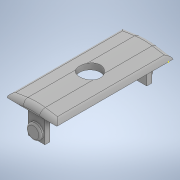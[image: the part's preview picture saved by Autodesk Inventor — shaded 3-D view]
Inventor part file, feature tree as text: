
AUTODESK INVENTOR PART (.ipt)
format: ipt  version: 2022 (Build 260153000, 153)  size: 212,480 bytes
history: native  units: mm
features: sketch x6, extrude x5, fillet x3, chamfer x2, mirror x1
ambient origin geometry x8: Origin, YZ Plane, XZ Plane, XY Plane, X Axis, Y Axis, Z Axis, Center Point
bodies: Solid1 (feature_tree)
feature tree (17):
  extrude  "Extrusion1"  Depth=70.0mm
  chamfer  "Chamfer1"  Distance=4.0mm
  chamfer  "Chamfer2"  Distance=2.0mm Angle=45.0deg
  fillet  "Fillet1"  Radius=35.0mm
  fillet  "Fillet2"  Radius=3.0mm
  extrude  "Extrusion2"  Depth=6.2mm
  extrude  "Extrusion3"  Depth=1.0mm
  extrude  "Extrusion4"  Depth=3.0mm
  fillet  "Fillet3"  Radius=10.0mm
  extrude  "Extrusion5"  Depth=5.0mm
  mirror  "Mirror1"
  sketch  "Sketch6"  dims[d23=16.0mm d24=0.0mm d25=5.0mm d26=2.0mm d27=8.8mm d28=2.0mm d29=0.0mm d30=1.0mm d31=0.0mm d32=0.0mm]
  sketch  "Sketch1"  dims[d0=30.0mm d1=70.0mm d2=4.0mm d3=0.0mm d4=13.25mm d5=2.0mm d6=45.0deg]
  sketch  "Sketch2"  dims[d7=13.25mm d8=2.0mm d9=45.0deg d10=35.0mm d11=3.0mm]
  sketch  "Sketch3"  dims[d13=4.0mm d14=0.0mm d16=6.2mm]
  sketch  "Sketch4"  dims[d18=33.0mm d19=1.0mm]
  sketch  "Sketch5"  dims[d20=5.0mm d21=3.0mm d22=10.0mm]
